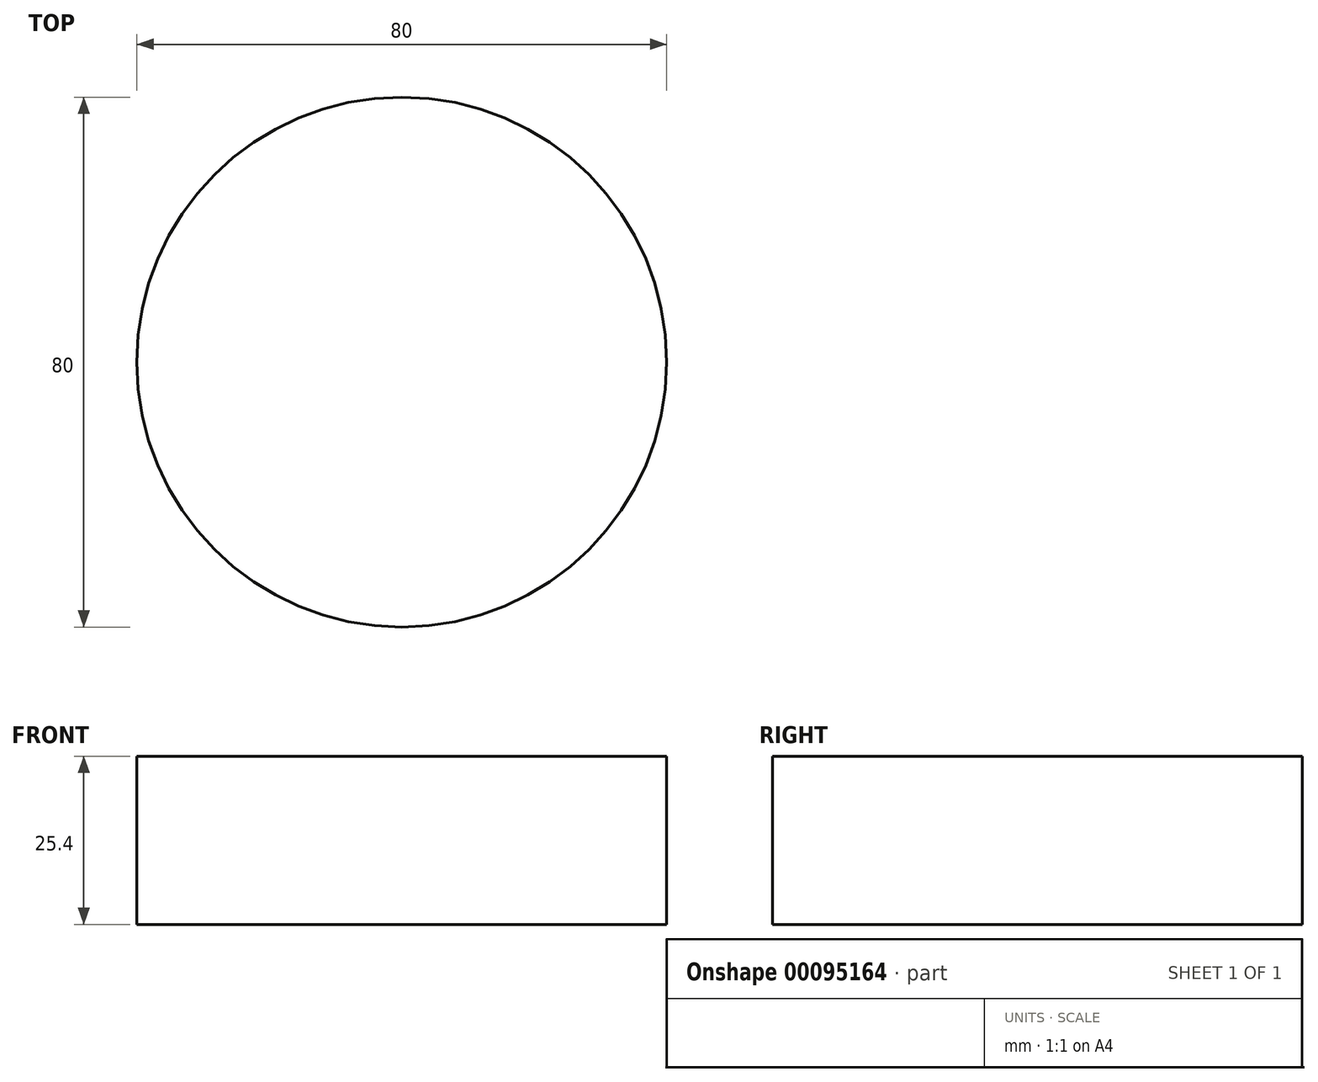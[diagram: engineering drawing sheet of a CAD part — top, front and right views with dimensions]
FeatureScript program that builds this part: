
annotation { "Feature Type Name" : "Feature", "Feature Type Description" : "" }
export const myFeature = defineFeature(function(context is Context, id is Id, definition is map)
    precondition{}
    {
        {
            var Q0;
            Q0=qCreatedBy(makeId("Top.planeOp"),FACE);
            var sketch = newSketch(context, id + "F0", { "sketchPlane" : qUnion([Q0])});
            skCircle(sketch, "E0", {"center": v(0, 0) * mm, "radius": 40 * mm});
            skSolve(sketch);
        }
        {
            var Q0;
            Q0=makeQuery(id+"F0.imprint","IMPRINT",FACE,{"disambiguationData":[TD([[makeQuery(id+"F0.imprint","IMPRINT",EDGE,{"derivedFrom":sQuery(id+"F0.wireOp",EDGE,"E0")}),1.0]])]});
            extrude(context, id + "F1", {"entities" : qUnion([Q0]), "depth" : 25.4 * mm});
        }
    });
